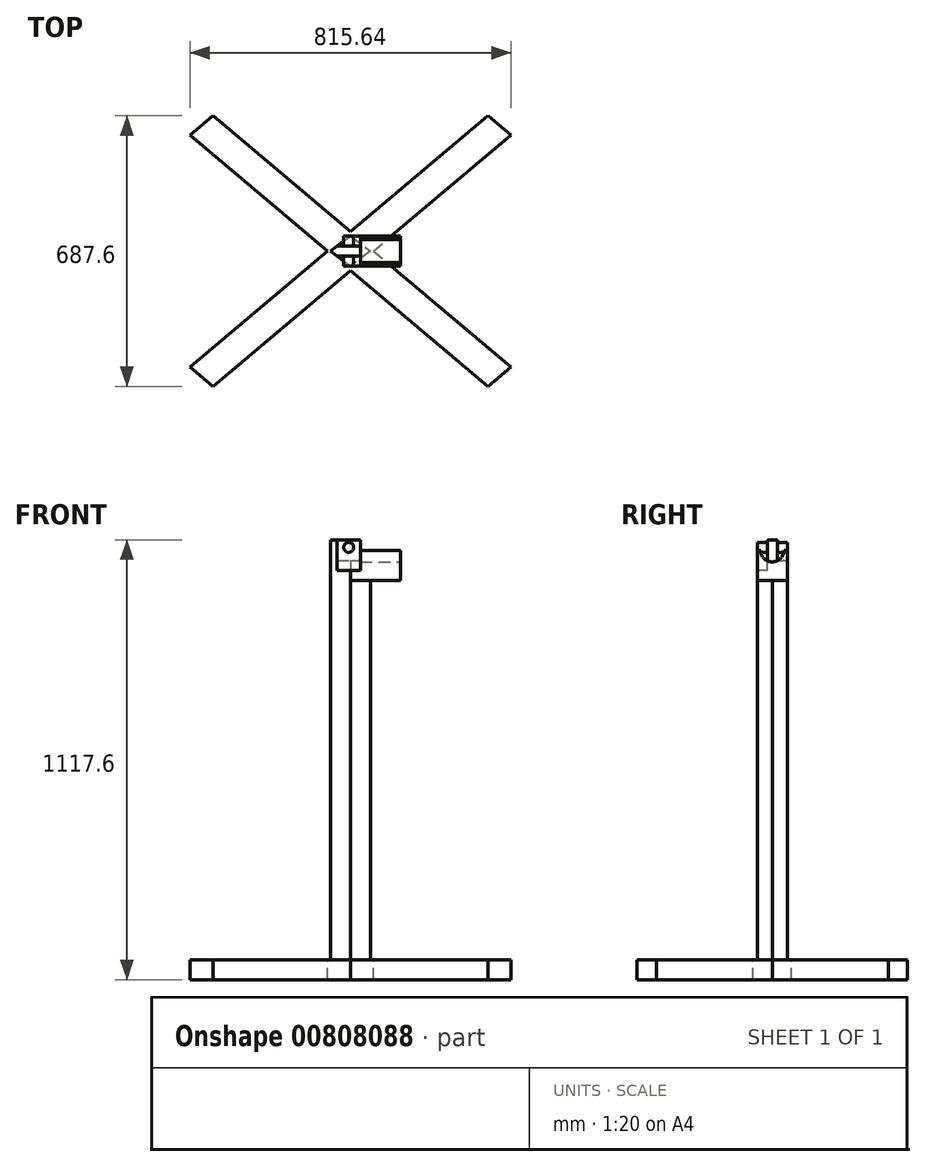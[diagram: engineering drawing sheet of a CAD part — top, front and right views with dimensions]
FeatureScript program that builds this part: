
annotation { "Feature Type Name" : "Feature", "Feature Type Description" : "" }
export const myFeature = defineFeature(function(context is Context, id is Id, definition is map)
    precondition{}
    {
        {
            var Q0;
            Q0=qCreatedBy(makeId("Top.planeOp"),FACE);
            var sketch = newSketch(context, id + "F0", { "sketchPlane" : qUnion([Q0])});
            skPoint(sketch, "E0.middle", {"position": v(0, 0) * mm});
            skLineSegment(sketch, "E1", {"start": v(282.37, -288.57) * mm, "end": v(-67.19, 6.12) * mm});
            skLineSegment(sketch, "E2", {"start": v(-475.01, 349.91) * mm, "end": v(-416.75, 399.03) * mm});
            skLineSegment(sketch, "E3", {"start": v(-416.75, 399.03) * mm, "end": v(-67.19, 104.34) * mm});
            skLineSegment(sketch, "E4", {"start": v(-475.01, -239.45) * mm, "end": v(-416.75, -288.57) * mm});
            skLineSegment(sketch, "E5", {"start": v(-416.75, -288.57) * mm, "end": v(-67.19, 6.12) * mm});
            skLineSegment(sketch, "E6", {"start": v(340.63, 349.91) * mm, "end": v(282.37, 399.03) * mm});
            skLineSegment(sketch, "E7", {"start": v(282.37, 399.03) * mm, "end": v(-67.19, 104.34) * mm});
            skLineSegment(sketch, "E8", {"start": v(282.37, -288.57) * mm, "end": v(340.63, -239.45) * mm});
            skLineSegment(sketch, "E9.trimOffspring", {"start": v(-8.93, 55.23) * mm, "end": v(340.63, -239.45) * mm});
            skLineSegment(sketch, "E10.trimOffspring", {"start": v(-125.45, 55.23) * mm, "end": v(-475.01, -239.45) * mm});
            skLineSegment(sketch, "E11.trimOffspring", {"start": v(-125.45, 55.23) * mm, "end": v(-475.01, 349.91) * mm});
            skLineSegment(sketch, "E12.trimOffspring", {"start": v(-8.93, 55.23) * mm, "end": v(340.63, 349.91) * mm});
            skSolve(sketch);
        }
        {
            var Q0;
            Q0 = qSketchRegion(id + "F0", true);
            extrude(context, id + "F1", {"entities" : qUnion([Q0]), "oppositeDirection" : true, "depth" : 50.8 * mm, "offsetDistance" : 25.4 * mm});
        }
        {
            var Q0;
            Q0=makeQuery(id+"F1.opExtrude","CAP_FACE",FACE,{"disambiguationData":[OSD([sQuery(id+"F0.wireOp",EDGE,"E1"),sQuery(id+"F0.wireOp",EDGE,"E2"),sQuery(id+"F0.wireOp",EDGE,"E3"),sQuery(id+"F0.wireOp",EDGE,"E4"),sQuery(id+"F0.wireOp",EDGE,"E5"),sQuery(id+"F0.wireOp",EDGE,"E6"),sQuery(id+"F0.wireOp",EDGE,"E7"),sQuery(id+"F0.wireOp",EDGE,"E8"),sQuery(id+"F0.wireOp",EDGE,"E9.trimOffspring"),sQuery(id+"F0.wireOp",EDGE,"E10.trimOffspring"),sQuery(id+"F0.wireOp",EDGE,"E11.trimOffspring"),sQuery(id+"F0.wireOp",EDGE,"E12.trimOffspring")])],"isStart":true});
            var sketch = newSketch(context, id + "F2", { "sketchPlane" : qUnion([Q0])});
            skLineSegment(sketch, "E13", {"start": v(-125.45, 55.23) * mm, "end": v(-8.93, 55.23) * mm, "construction": true});
            skLineSegment(sketch, "E14", {"start": v(-67.19, 104.34) * mm, "end": v(-67.19, 6.12) * mm, "construction": true});
            skPoint(sketch, "E15.middle", {"position": v(-67.19, 55.23) * mm});
            skLineSegment(sketch, "E16", {"start": v(-117.99, 55.23) * mm, "end": v(-67.19, 93.33) * mm});
            skLineSegment(sketch, "E17", {"start": v(-67.19, 93.33) * mm, "end": v(-16.39, 55.23) * mm});
            skLineSegment(sketch, "E18", {"start": v(-16.39, 55.23) * mm, "end": v(-67.19, 17.13) * mm});
            skLineSegment(sketch, "E19", {"start": v(-67.19, 17.13) * mm, "end": v(-117.99, 55.23) * mm});
            skSolve(sketch);
        }
        {
            var Q0;
            {var subQ0=sQuery(id+"F2.wireOp",EDGE,"wgdWIPvC-I4hR-T0Zt-xnxe-Nl3ozaKQzP4W");var subQ1=makeQuery(id+"F2.imprint","INTERSECT",VERTEX,{"derivedFrom":[makeQuery(id+"F1.opExtrude","CAP_EDGE",EDGE,{"disambiguationData":[OSD([sQuery(id+"F0.wireOp",EDGE,"E1")])],"isStart":true}),makeQuery(id+"F1.opExtrude","CAP_EDGE",EDGE,{"disambiguationData":[OSD([sQuery(id+"F0.wireOp",EDGE,"E5")])],"isStart":true}),subQ0]});Q0=makeQuery(id+"F2.imprint","IMPRINT",FACE,{"disambiguationData":[TD([[makeQuery(id+"F2.imprint","IMPRINT",EDGE,{"disambiguationData":[TD([[subQ1,1.0]])],"derivedFrom":subQ0}),1.0]])]});}
            var Q1;
            Q1=makeQuery(id+"F2.imprint","IMPRINT",FACE,{"disambiguationData":[TD([[makeQuery(id+"F2.imprint","IMPRINT",EDGE,{"derivedFrom":sQuery(id+"F2.wireOp",EDGE,"VLmX2QcA-QAkb-Bhdo-7lbi-0TtQg2hfHBJQ")}),-1.0]])]});
            var Q2;
            Q2=makeQuery(id+"F2.imprint","IMPRINT",FACE,{"disambiguationData":[TD([[makeQuery(id+"F2.imprint","IMPRINT",EDGE,{"derivedFrom":sQuery(id+"F2.wireOp",EDGE,"E16")}),-1.0]])]});
            extrude(context, id + "F3", {"entities" : qUnion([Q0, Q1, Q2]), "operationType" : NewBodyOperationType.ADD, "depth" : 1066.8 * mm, "offsetDistance" : 25.4 * mm});
        }
        {
            var Q0;
            Q0=makeQuery(id+"F3.opExtrude","CAP_FACE",FACE,{"disambiguationData":[OSD([sQuery(id+"F2.wireOp",EDGE,"E16"),sQuery(id+"F2.wireOp",EDGE,"E17"),sQuery(id+"F2.wireOp",EDGE,"E18"),sQuery(id+"F2.wireOp",EDGE,"E19")])],"isStart":false});
            var sketch = newSketch(context, id + "F4", { "sketchPlane" : qUnion([Q0])});
            skLineSegment(sketch, "E20.top", {"start": v(-28.53, 103.17) * mm, "end": v(-104.72, 103.17) * mm});
            skLineSegment(sketch, "E20.left", {"start": v(-28.53, 67.93) * mm, "end": v(-28.53, 103.17) * mm});
            skLineSegment(sketch, "E20.right", {"start": v(-104.72, 67.93) * mm, "end": v(-104.72, 103.17) * mm});
            skLineSegment(sketch, "E21.bottom", {"start": v(-104.45, 42.53) * mm, "end": v(-29.62, 42.53) * mm});
            skLineSegment(sketch, "E21.top", {"start": v(-104.45, 3.33) * mm, "end": v(-29.62, 3.33) * mm});
            skLineSegment(sketch, "E21.left", {"start": v(-104.45, 42.53) * mm, "end": v(-104.45, 3.33) * mm});
            skLineSegment(sketch, "E21.right", {"start": v(-29.62, 42.53) * mm, "end": v(-29.62, 3.33) * mm});
            skLineSegment(sketch, "E22", {"start": v(-117.99, 55.23) * mm, "end": v(-16.39, 55.23) * mm, "construction": true});
            skLineSegment(sketch, "E23", {"start": v(-104.72, 67.93) * mm, "end": v(-28.53, 67.93) * mm});
            skSolve(sketch);
        }
        {
            var Q0;
            {var subQ0=sQuery(id+"F4.wireOp",EDGE,"E21.bottom");var subQ1=makeQuery(id+"F3.opExtrude","CAP_EDGE",EDGE,{"disambiguationData":[OSD([sQuery(id+"F2.wireOp",EDGE,"E19")])],"isStart":false});var subQ2=makeQuery(id+"F4.imprint","INTERSECT",VERTEX,{"derivedFrom":[subQ1,subQ0]});Q0=makeQuery(id+"F4.imprint","IMPRINT",FACE,{"disambiguationData":[TD([[makeQuery(id+"F4.imprint","IMPRINT",EDGE,{"disambiguationData":[TD([[subQ2,-1.0]])],"derivedFrom":subQ0}),-1.0]])]});}
            var Q1;
            {var subQ0=sQuery(id+"F4.wireOp",EDGE,"E20.bottom");var subQ1=makeQuery(id+"F3.opExtrude","CAP_EDGE",EDGE,{"disambiguationData":[OSD([sQuery(id+"F2.wireOp",EDGE,"E17")])],"isStart":false});var subQ2=makeQuery(id+"F4.imprint","INTERSECT",VERTEX,{"derivedFrom":[subQ1,subQ0]});Q1=makeQuery(id+"F4.imprint","IMPRINT",FACE,{"disambiguationData":[TD([[makeQuery(id+"F4.imprint","IMPRINT",EDGE,{"disambiguationData":[TD([[subQ2,-1.0]])],"derivedFrom":subQ0}),-1.0]])]});}
            var Q2;
            {var subQ0=sQuery(id+"F4.wireOp",EDGE,"E23");var subQ1=makeQuery(id+"F3.opExtrude","CAP_EDGE",EDGE,{"disambiguationData":[OSD([sQuery(id+"F2.wireOp",EDGE,"E16")])],"isStart":false});var subQ2=makeQuery(id+"F4.imprint","INTERSECT",VERTEX,{"derivedFrom":[subQ1,subQ0]});Q2=makeQuery(id+"F4.imprint","IMPRINT",FACE,{"disambiguationData":[TD([[makeQuery(id+"F4.imprint","IMPRINT",EDGE,{"disambiguationData":[TD([[subQ2,-1.0]])],"derivedFrom":subQ0}),1.0]])]});}
            extrude(context, id + "F5", {"entities" : qUnion([Q0, Q1, Q2]), "operationType" : NewBodyOperationType.REMOVE, "oppositeDirection" : true, "depth" : 26.67 * mm, "offsetDistance" : 25.4 * mm});
        }
        {
            var Q0;
            Q0=makeQuery(id+"F5.boolean.opBoolean","COPY",FACE,{"derivedFrom":makeQuery(id+"F5.opExtrude","CAP_FACE",FACE,{"disambiguationData":[OSD([sQuery(id+"F2.wireOp",EDGE,"E16"),sQuery(id+"F2.wireOp",EDGE,"E17"),sQuery(id+"F4.wireOp",EDGE,"E23")])],"isStart":false})});
            var sketch = newSketch(context, id + "F6", { "sketchPlane" : qUnion([Q0])});
            skLineSegment(sketch, "E24.0", {"start": v(-67.19, 93.33) * mm, "end": v(-33.32, 67.93) * mm});
            skLineSegment(sketch, "E25.0", {"start": v(-33.32, 67.93) * mm, "end": v(-16.39, 55.23) * mm});
            skLineSegment(sketch, "E26.0", {"start": v(-16.39, 55.23) * mm, "end": v(-33.32, 42.53) * mm});
            skLineSegment(sketch, "E27.0", {"start": v(-33.32, 42.53) * mm, "end": v(-67.19, 17.13) * mm});
            skLineSegment(sketch, "E28.bottom", {"start": v(-67.19, 93.33) * mm, "end": v(59.81, 93.33) * mm});
            skLineSegment(sketch, "E28.top", {"start": v(-67.19, 17.13) * mm, "end": v(59.81, 17.13) * mm});
            skLineSegment(sketch, "E28.right", {"start": v(59.81, 93.33) * mm, "end": v(59.81, 17.13) * mm});
            skSolve(sketch);
        }
        {
            var Q0;
            Q0=makeQuery(id+"F6.imprint","IMPRINT",FACE,{"disambiguationData":[TD([[makeQuery(id+"F6.imprint","IMPRINT",EDGE,{"derivedFrom":sQuery(id+"F6.wireOp",EDGE,"E24.0")}),1.0]])]});
            extrude(context, id + "F7", {"entities" : qUnion([Q0]), "operationType" : NewBodyOperationType.ADD, "oppositeDirection" : true, "depth" : 76.2 * mm, "offsetDistance" : 25.4 * mm});
        }
        {
            var Q0;
            Q0=makeQuery(id+"F7.opExtrude","SWEPT_FACE",FACE,{"disambiguationData":[OSD([sQuery(id+"F6.wireOp",EDGE,"E28.right")])]});
            var sketch = newSketch(context, id + "F8", { "sketchPlane" : qUnion([Q0])});
            skCircle(sketch, "E29", {"center": v(55.23, 1040.13) * mm, "radius": 29.21 * mm});
            skSolve(sketch);
        }
        {
            var Q0;
            Q0 = qSketchRegion(id + "F8", true);
            extrude(context, id + "F9", {"entities" : qUnion([Q0]), "operationType" : NewBodyOperationType.REMOVE, "oppositeDirection" : true, "depth" : 101.6 * mm, "offsetDistance" : 25.4 * mm});
        }
        {
            var Q0;
            Q0=makeQuery(id+"F3.opExtrude","CAP_FACE",FACE,{"disambiguationData":[OSD([sQuery(id+"F2.wireOp",EDGE,"E16"),sQuery(id+"F2.wireOp",EDGE,"E17"),sQuery(id+"F2.wireOp",EDGE,"E18"),sQuery(id+"F2.wireOp",EDGE,"E19")])],"isStart":false});
            var sketch = newSketch(context, id + "F10", { "sketchPlane" : qUnion([Q0])});
            skLineSegment(sketch, "E30.0", {"start": v(-41.79, 67.93) * mm, "end": v(-33.32, 67.93) * mm});
            skLineSegment(sketch, "E31.0", {"start": v(-33.32, 67.93) * mm, "end": v(-16.39, 55.23) * mm});
            skLineSegment(sketch, "E32.0", {"start": v(-16.39, 55.23) * mm, "end": v(-33.32, 42.53) * mm});
            skLineSegment(sketch, "E33.0", {"start": v(-41.79, 42.53) * mm, "end": v(-33.32, 42.53) * mm});
            skLineSegment(sketch, "E34", {"start": v(-41.79, 67.93) * mm, "end": v(-41.79, 42.53) * mm});
            skPoint(sketch, "E35.orphan", {"position": v(-101.06, 67.93) * mm});
            skPoint(sketch, "E36.orphan", {"position": v(-101.06, 42.53) * mm});
            skPoint(sketch, "E37.0.end.orphan", {"position": v(-41.79, 84.44) * mm});
            skSolve(sketch);
        }
        {
            var Q0;
            Q0=makeQuery(id+"F10.imprint","IMPRINT",FACE,{"disambiguationData":[TD([[makeQuery(id+"F10.imprint","IMPRINT",EDGE,{"derivedFrom":sQuery(id+"F10.wireOp",EDGE,"E30.0")}),-1.0]])]});
            var Q1;
            {var subQ0=sQuery(id+"F10.wireOp",EDGE,"E33.0");Q1=makeQuery(id+"F10.imprint","IMPRINT",FACE,{"disambiguationData":[TD([[makeQuery(id+"F10.imprint","IMPRINT",EDGE,{"derivedFrom":subQ0}),1.0]])]});}
            extrude(context, id + "F11", {"entities" : qUnion([Q0, Q1]), "operationType" : NewBodyOperationType.REMOVE, "endBound" : BoundingType.UP_TO_NEXT, "oppositeDirection" : true, "depth" : 50.8 * mm, "offsetDistance" : 25.4 * mm});
        }
        {
            var Q0;
            Q0=makeQuery(id+"F9.boolean.opBoolean","COPY",FACE,{"derivedFrom":makeQuery(id+"F9.opExtrude","CAP_FACE",FACE,{"disambiguationData":[OSD([sQuery(id+"F8.wireOp",EDGE,"E29")])],"isStart":false})});
            var sketch = newSketch(context, id + "F12", { "sketchPlane" : qUnion([Q0])});
            skLineSegment(sketch, "E38.0", {"start": v(26.02, 1040.13) * mm, "end": v(42.53, 1040.13) * mm});
            skLineSegment(sketch, "E39.0", {"start": v(67.93, 1040.13) * mm, "end": v(84.44, 1040.13) * mm});
            skArc(sketch, "E40.0", {"start": v(26.02, 1040.13) * mm, "mid": v(30.49, 1024.6) * mm, "end": v(42.53, 1013.83) * mm});
            skLineSegment(sketch, "E41", {"start": v(42.53, 1040.13) * mm, "end": v(42.53, 1013.83) * mm});
            skLineSegment(sketch, "E42", {"start": v(67.93, 1040.13) * mm, "end": v(67.93, 1013.83) * mm});
            skArc(sketch, "E43.trimOffspring", {"start": v(67.93, 1013.83) * mm, "mid": v(79.97, 1024.6) * mm, "end": v(84.44, 1040.13) * mm});
            skSolve(sketch);
        }
        {
            var Q0;
            Q0 = qSketchRegion(id + "F12", true);
            extrude(context, id + "F13", {"entities" : qUnion([Q0]), "operationType" : NewBodyOperationType.REMOVE, "endBound" : BoundingType.UP_TO_NEXT, "oppositeDirection" : true, "depth" : 25.4 * mm, "offsetDistance" : 25.4 * mm});
        }
        {
            var Q0;
            Q0=makeQuery(id+"F7.opExtrude","SWEPT_FACE",FACE,{"disambiguationData":[OSD([sQuery(id+"F6.wireOp",EDGE,"E28.top")])]});
            var sketch = newSketch(context, id + "F14", { "sketchPlane" : qUnion([Q0])});
            skLineSegment(sketch, "E44.0", {"start": v(-67.19, 1040.13) * mm, "end": v(-41.79, 1040.13) * mm});
            skPoint(sketch, "E45.orphan", {"position": v(59.81, 1040.13) * mm});
            skPoint(sketch, "E46.orphan", {"position": v(-41.79, 1066.8) * mm});
            skLineSegment(sketch, "E47", {"start": v(-67.19, 1040.13) * mm, "end": v(-101.06, 1040.13) * mm});
            skPoint(sketch, "E48.orphan", {"position": v(-101.06, 1066.8) * mm});
            skLineSegment(sketch, "E49.top", {"start": v(-101.06, 989.33) * mm, "end": v(-41.79, 989.33) * mm});
            skLineSegment(sketch, "E50", {"start": v(-101.06, 989.33) * mm, "end": v(-101.06, 1040.13) * mm});
            skLineSegment(sketch, "E51", {"start": v(-41.79, 989.33) * mm, "end": v(-41.79, 1040.13) * mm});
            skSolve(sketch);
        }
        {
            var Q0;
            {var subQ0=sQuery(id+"F14.wireOp",EDGE,"91e3f64d-cfc5-48aa-956f-56200beb85da.0");Q0=makeQuery(id+"F14.imprint","IMPRINT",FACE,{"disambiguationData":[TD([[makeQuery(id+"F14.imprint","IMPRINT",EDGE,{"derivedFrom":subQ0}),-1.0]])]});}
            var Q1;
            {var subQ0=sQuery(id+"F14.wireOp",EDGE,"3b4ab840-8c4a-4b07-9c90-480e8c33c28e.0");Q1=makeQuery(id+"F14.imprint","IMPRINT",FACE,{"disambiguationData":[TD([[makeQuery(id+"F14.imprint","IMPRINT",EDGE,{"derivedFrom":subQ0}),1.0]])]});}
            var Q2;
            {var subQ0=sQuery(id+"F14.wireOp",EDGE,"E47");Q2=makeQuery(id+"F14.imprint","IMPRINT",FACE,{"disambiguationData":[TD([[makeQuery(id+"F14.imprint","IMPRINT",EDGE,{"derivedFrom":subQ0}),1.0]])]});}
            var Q3;
            {var subQ0=sQuery(id+"F14.wireOp",EDGE,"E44.0");Q3=makeQuery(id+"F14.imprint","IMPRINT",FACE,{"disambiguationData":[TD([[makeQuery(id+"F14.imprint","IMPRINT",EDGE,{"derivedFrom":subQ0}),-1.0]])]});}
            var Q4;
            Q4=makeQuery(id+"F13.boolean.opBoolean","MERGE",FACE,{"derivedFrom":[makeQuery(id+"F5.boolean.opBoolean","COPY",FACE,{"derivedFrom":makeQuery(id+"F5.opExtrude","SWEPT_FACE",FACE,{"disambiguationData":[OSD([sQuery(id+"F4.wireOp",EDGE,"E21.bottom")])]})}),makeQuery(id+"F13.opExtrude","SWEPT_FACE",FACE,{"disambiguationData":[OSD([sQuery(id+"F12.wireOp",EDGE,"E41")])]})]});
            extrude(context, id + "F15", {"entities" : qUnion([Q0, Q1, Q2, Q3]), "operationType" : NewBodyOperationType.REMOVE, "oppositeDirection" : true, "depth" : 25.4 * mm, "endBoundEntityFace" : qUnion([Q4]), "offsetDistance" : 25.4 * mm});
        }
        {
            var Q0;
            Q0=makeQuery(id+"F7.opExtrude","SWEPT_FACE",FACE,{"disambiguationData":[OSD([sQuery(id+"F6.wireOp",EDGE,"E28.bottom")])]});
            var sketch = newSketch(context, id + "F16", { "sketchPlane" : qUnion([Q0])});
            skLineSegment(sketch, "E52.0", {"start": v(41.79, 1013.83) * mm, "end": v(41.79, 1040.13) * mm});
            skLineSegment(sketch, "E53.0", {"start": v(101.06, 1013.83) * mm, "end": v(41.79, 1013.83) * mm});
            skLineSegment(sketch, "E54.0", {"start": v(101.06, 1013.83) * mm, "end": v(101.06, 1040.13) * mm});
            skLineSegment(sketch, "E55.0", {"start": v(67.19, 1040.13) * mm, "end": v(41.79, 1040.13) * mm});
            skLineSegment(sketch, "E56", {"start": v(67.19, 1040.13) * mm, "end": v(101.06, 1040.13) * mm});
            skPoint(sketch, "E57.orphan", {"position": v(41.79, 1066.8) * mm});
            skPoint(sketch, "E58.orphan", {"position": v(101.06, 1066.8) * mm});
            skPoint(sketch, "E59.orphan", {"position": v(-59.81, 1040.13) * mm});
            skSolve(sketch);
        }
        {
            var Q0;
            {var subQ0=sQuery(id+"F16.wireOp",EDGE,"E54.0");Q0=makeQuery(id+"F16.imprint","IMPRINT",FACE,{"disambiguationData":[TD([[makeQuery(id+"F16.imprint","IMPRINT",EDGE,{"derivedFrom":subQ0}),1.0]])]});}
            var Q1;
            {var subQ0=sQuery(id+"F16.wireOp",EDGE,"E52.0");Q1=makeQuery(id+"F16.imprint","IMPRINT",FACE,{"disambiguationData":[TD([[makeQuery(id+"F16.imprint","IMPRINT",EDGE,{"derivedFrom":subQ0}),-1.0]])]});}
            extrude(context, id + "F17", {"entities" : qUnion([Q0, Q1]), "operationType" : NewBodyOperationType.REMOVE, "oppositeDirection" : true, "depth" : 25.4 * mm, "offsetDistance" : 25.4 * mm});
        }
        {
            var Q0;
            Q0=makeQuery(id+"F13.boolean.opBoolean","MERGE",FACE,{"derivedFrom":[makeQuery(id+"F5.boolean.opBoolean","COPY",FACE,{"derivedFrom":makeQuery(id+"F5.opExtrude","SWEPT_FACE",FACE,{"disambiguationData":[OSD([sQuery(id+"F4.wireOp",EDGE,"E21.bottom")])]})}),makeQuery(id+"F13.opExtrude","SWEPT_FACE",FACE,{"disambiguationData":[OSD([sQuery(id+"F12.wireOp",EDGE,"E41")])]})]});
            var sketch = newSketch(context, id + "F18", { "sketchPlane" : qUnion([Q0])});
            skCircle(sketch, "E60", {"center": v(-71.42, 1047.75) * mm, "radius": 12.7 * mm});
            skPoint(sketch, "E60.centerSnap0", {"position": v(-71.42, 1066.8) * mm});
            skSolve(sketch);
        }
        {
            var Q0;
            Q0=makeQuery(id+"F18.imprint","IMPRINT",FACE,{"disambiguationData":[TD([[makeQuery(id+"F18.imprint","IMPRINT",EDGE,{"derivedFrom":sQuery(id+"F18.wireOp",EDGE,"E60")}),1.0]])]});
            extrude(context, id + "F19", {"entities" : qUnion([Q0]), "operationType" : NewBodyOperationType.ADD, "depth" : 25.4 * mm, "offsetDistance" : 25.4 * mm, "hasSecondDirection" : true, "secondDirectionOppositeDirection" : true, "secondDirectionDepth" : 50.8 * mm});
        }
    });
